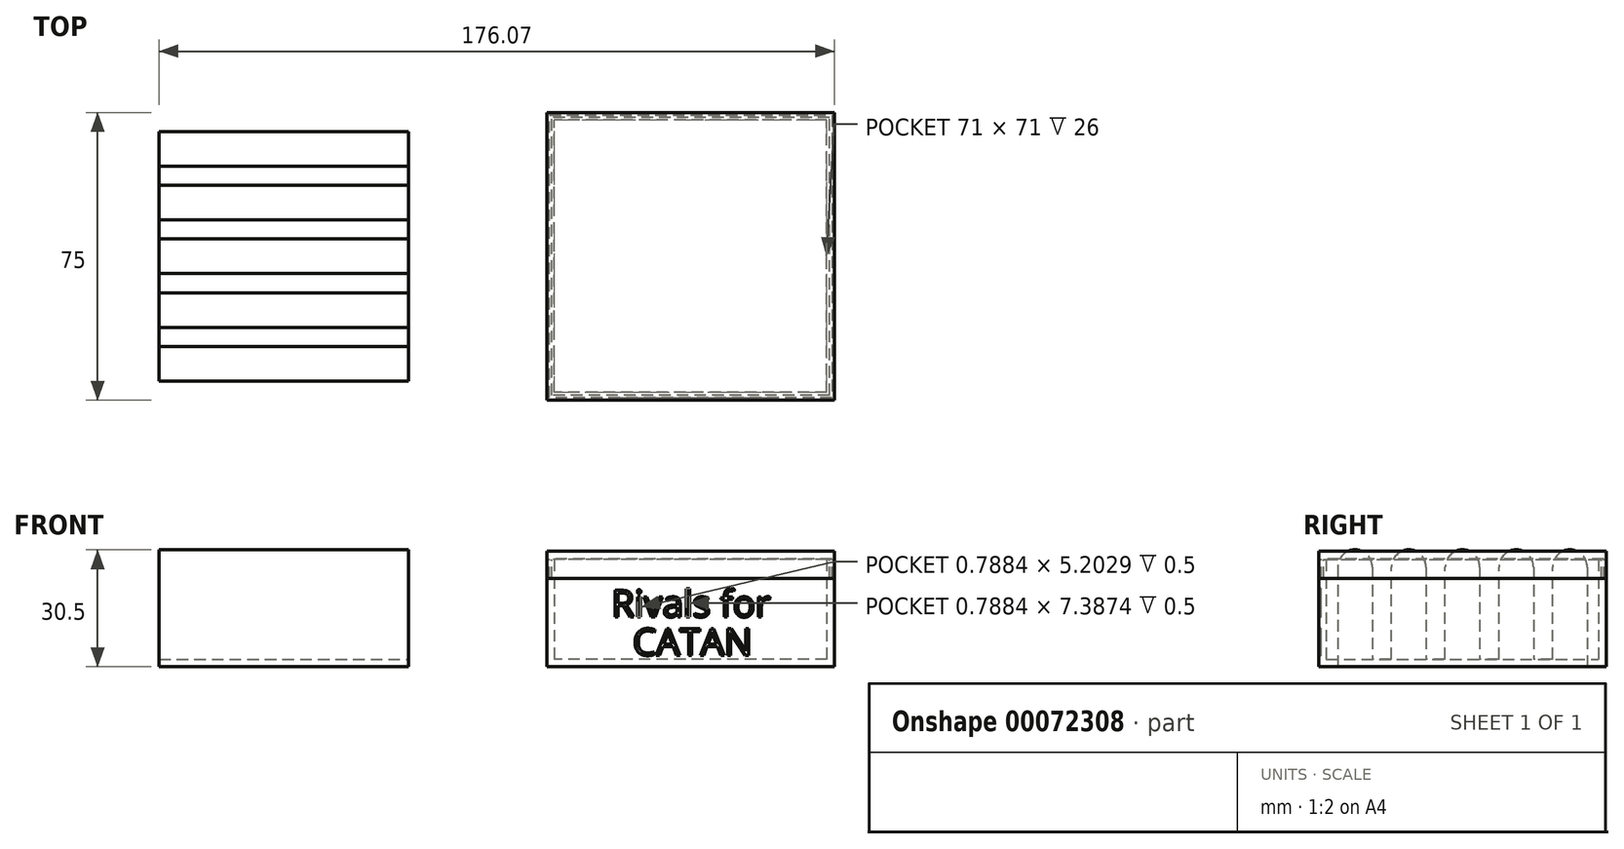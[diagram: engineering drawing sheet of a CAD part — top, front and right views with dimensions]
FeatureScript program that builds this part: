
annotation { "Feature Type Name" : "Feature", "Feature Type Description" : "" }
export const myFeature = defineFeature(function(context is Context, id is Id, definition is map)
    precondition{}
    {
        {
            var Q0;
            Q0=qCreatedBy(makeId("Top.planeOp"),FACE);
            var sketch = newSketch(context, id + "F0", { "sketchPlane" : qUnion([Q0])});
            skLineSegment(sketch, "E0.rect.bottom", {"start": v(37.5, -37.5) * mm, "end": v(-37.5, -37.5) * mm});
            skLineSegment(sketch, "E0.rect.top", {"start": v(37.5, 37.5) * mm, "end": v(-37.5, 37.5) * mm});
            skLineSegment(sketch, "E0.rect.left", {"start": v(37.5, -37.5) * mm, "end": v(37.5, 37.5) * mm});
            skLineSegment(sketch, "E0.rect.right", {"start": v(-37.5, -37.5) * mm, "end": v(-37.5, 37.5) * mm});
            skPoint(sketch, "E0.rect.middle", {"position": v(0, 0) * mm});
            skLineSegment(sketch, "E1", {"start": v(-37.5, 37.5) * mm, "end": v(37.5, -37.5) * mm, "construction": true});
            skLineSegment(sketch, "E2", {"start": v(0, 0) * mm, "end": v(-106.07, 0) * mm, "construction": true});
            skLineSegment(sketch, "E3.rect.bottom", {"start": v(-73.57, 32.5) * mm, "end": v(-138.57, 32.5) * mm});
            skLineSegment(sketch, "E3.rect.top", {"start": v(-73.57, -32.5) * mm, "end": v(-138.57, -32.5) * mm});
            skLineSegment(sketch, "E3.rect.left", {"start": v(-73.57, 32.5) * mm, "end": v(-73.57, -32.5) * mm});
            skLineSegment(sketch, "E3.rect.right", {"start": v(-138.57, 32.5) * mm, "end": v(-138.57, -32.5) * mm});
            skPoint(sketch, "E3.rect.middle", {"position": v(-106.07, 0) * mm});
            skSolve(sketch);
        }
        {
            var Q0;
            Q0 = qSketchRegion(id + "F0", true);
            extrude(context, id + "F1", {"entities" : qUnion([Q0]), "depth" : 2 * mm});
        }
        {
            var Q0;
            Q0=makeQuery(id+"F1.opExtrude","CAP_FACE",FACE,{"disambiguationData":[OSD([sQuery(id+"F0.wireOp",EDGE,"E0.rect.bottom"),sQuery(id+"F0.wireOp",EDGE,"E0.rect.top"),sQuery(id+"F0.wireOp",EDGE,"E0.rect.left"),sQuery(id+"F0.wireOp",EDGE,"E0.rect.right")])],"isStart":false});
            var sketch = newSketch(context, id + "F2", { "sketchPlane" : qUnion([Q0])});
            skLineSegment(sketch, "E4.rect.bottom", {"start": v(35.5, -35.5) * mm, "end": v(-35.5, -35.5) * mm});
            skLineSegment(sketch, "E4.rect.top", {"start": v(35.5, 35.5) * mm, "end": v(-35.5, 35.5) * mm});
            skLineSegment(sketch, "E4.rect.left", {"start": v(35.5, -35.5) * mm, "end": v(35.5, 35.5) * mm});
            skLineSegment(sketch, "E4.rect.right", {"start": v(-35.5, -35.5) * mm, "end": v(-35.5, 35.5) * mm});
            skPoint(sketch, "E4.rect.middle", {"position": v(0, 0) * mm});
            skLineSegment(sketch, "E5.0.0", {"start": v(-37.5, -37.5) * mm, "end": v(37.5, -37.5) * mm});
            skLineSegment(sketch, "E5.0.1", {"start": v(37.5, -37.5) * mm, "end": v(37.5, 37.5) * mm});
            skLineSegment(sketch, "E5.0.2", {"start": v(37.5, 37.5) * mm, "end": v(-37.5, 37.5) * mm});
            skLineSegment(sketch, "E5.0.3", {"start": v(-37.5, 37.5) * mm, "end": v(-37.5, -37.5) * mm});
            skLineSegment(sketch, "E6", {"start": v(0, 35.5) * mm, "end": v(0, 37.5) * mm, "construction": true});
            skSolve(sketch);
        }
        {
            var Q0;
            Q0 = qSketchRegion(id + "F2", true);
            extrude(context, id + "F3", {"entities" : qUnion([Q0]), "operationType" : NewBodyOperationType.ADD, "depth" : 26 * mm});
        }
        {
            var Q0;
            Q0=makeQuery(id+"F3.opExtrude","CAP_FACE",FACE,{"disambiguationData":[OSD([sQuery(id+"F2.wireOp",EDGE,"E4.rect.bottom"),sQuery(id+"F2.wireOp",EDGE,"E4.rect.top"),sQuery(id+"F2.wireOp",EDGE,"E4.rect.left"),sQuery(id+"F2.wireOp",EDGE,"E4.rect.right"),sQuery(id+"F2.wireOp",EDGE,"E5.0.0"),sQuery(id+"F2.wireOp",EDGE,"E5.0.1"),sQuery(id+"F2.wireOp",EDGE,"E5.0.2"),sQuery(id+"F2.wireOp",EDGE,"E5.0.3")])],"isStart":false});
            var sketch = newSketch(context, id + "F4", { "sketchPlane" : qUnion([Q0])});
            skLineSegment(sketch, "E7.0", {"start": v(-37.5, -37.5) * mm, "end": v(-37.5, 37.5) * mm});
            skLineSegment(sketch, "E8.0", {"start": v(37.5, -37.5) * mm, "end": v(-37.5, -37.5) * mm});
            skLineSegment(sketch, "E9.0", {"start": v(37.5, -37.5) * mm, "end": v(37.5, 37.5) * mm});
            skLineSegment(sketch, "E10.0", {"start": v(37.5, 37.5) * mm, "end": v(-37.5, 37.5) * mm});
            skLineSegment(sketch, "E11.0", {"start": v(-36.2, -36.2) * mm, "end": v(-36.2, 36.2) * mm});
            skLineSegment(sketch, "E11.1", {"start": v(36.2, -36.2) * mm, "end": v(-36.2, -36.2) * mm});
            skLineSegment(sketch, "E11.2", {"start": v(36.2, -36.2) * mm, "end": v(36.2, 36.2) * mm});
            skLineSegment(sketch, "E11.3", {"start": v(36.2, 36.2) * mm, "end": v(-36.2, 36.2) * mm});
            skSolve(sketch);
        }
        {
            var Q0;
            Q0 = qSketchRegion(id + "F4", true);
            extrude(context, id + "F5", {"entities" : qUnion([Q0]), "operationType" : NewBodyOperationType.REMOVE, "oppositeDirection" : true, "depth" : 5 * mm});
        }
        {
            var Q0;
            Q0=makeQuery(id+"F3.opExtrude","CAP_FACE",FACE,{"disambiguationData":[OSD([sQuery(id+"F2.wireOp",EDGE,"E4.rect.bottom"),sQuery(id+"F2.wireOp",EDGE,"E4.rect.top"),sQuery(id+"F2.wireOp",EDGE,"E4.rect.left"),sQuery(id+"F2.wireOp",EDGE,"E4.rect.right"),sQuery(id+"F2.wireOp",EDGE,"E5.0.0"),sQuery(id+"F2.wireOp",EDGE,"E5.0.1"),sQuery(id+"F2.wireOp",EDGE,"E5.0.2"),sQuery(id+"F2.wireOp",EDGE,"E5.0.3")])],"isStart":false});
            cPlane(context, id + "F6", {"entities" : qUnion([Q0]), "cplaneType" : CPlaneType.OFFSET, "offset" : .1 * mm, "width" : 150 * mm, "height" : 150 * mm});
        }
        {
            var Q0;
            Q0=qCreatedBy(id+"F6.planeOp",FACE);
            var sketch = newSketch(context, id + "F7", { "sketchPlane" : qUnion([Q0])});
            skPoint(sketch, "E12.0", {"position": v(37.5, -37.5) * mm});
            skLineSegment(sketch, "E13.rect.bottom", {"start": v(37.5, -37.5) * mm, "end": v(-37.5, -37.5) * mm});
            skLineSegment(sketch, "E13.rect.top", {"start": v(37.5, 37.5) * mm, "end": v(-37.5, 37.5) * mm});
            skLineSegment(sketch, "E13.rect.left", {"start": v(37.5, -37.5) * mm, "end": v(37.5, 37.5) * mm});
            skLineSegment(sketch, "E13.rect.right", {"start": v(-37.5, -37.5) * mm, "end": v(-37.5, 37.5) * mm});
            skPoint(sketch, "E13.rect.middle", {"position": v(0, 0) * mm});
            skSolve(sketch);
        }
        {
            var Q0;
            Q0 = qSketchRegion(id + "F7", true);
            extrude(context, id + "F8", {"entities" : qUnion([Q0]), "depth" : 2 * mm});
        }
        {
            var Q0;
            Q0=makeQuery(id+"F8.opExtrude","CAP_FACE",FACE,{"disambiguationData":[OSD([sQuery(id+"F7.wireOp",EDGE,"E13.rect.bottom"),sQuery(id+"F7.wireOp",EDGE,"E13.rect.top"),sQuery(id+"F7.wireOp",EDGE,"E13.rect.left"),sQuery(id+"F7.wireOp",EDGE,"E13.rect.right")])],"isStart":true});
            var sketch = newSketch(context, id + "F9", { "sketchPlane" : qUnion([Q0])});
            skLineSegment(sketch, "E14.0.0", {"start": v(37.5, 37.5) * mm, "end": v(-37.5, 37.5) * mm});
            skLineSegment(sketch, "E14.0.1", {"start": v(-37.5, 37.5) * mm, "end": v(-37.5, -37.5) * mm});
            skLineSegment(sketch, "E14.0.2", {"start": v(-37.5, -37.5) * mm, "end": v(37.5, -37.5) * mm});
            skLineSegment(sketch, "E14.0.3", {"start": v(37.5, -37.5) * mm, "end": v(37.5, 37.5) * mm});
            skLineSegment(sketch, "E15.0", {"start": v(36.8, 36.8) * mm, "end": v(-36.8, 36.8) * mm});
            skLineSegment(sketch, "E15.1", {"start": v(36.8, -36.8) * mm, "end": v(36.8, 36.8) * mm});
            skLineSegment(sketch, "E15.2", {"start": v(-36.8, -36.8) * mm, "end": v(36.8, -36.8) * mm});
            skLineSegment(sketch, "E15.3", {"start": v(-36.8, 36.8) * mm, "end": v(-36.8, -36.8) * mm});
            skSolve(sketch);
        }
        {
            var Q0;
            Q0 = qSketchRegion(id + "F9", true);
            extrude(context, id + "F10", {"entities" : qUnion([Q0]), "operationType" : NewBodyOperationType.ADD, "depth" : 5 * mm});
        }
        {
            var Q0;
            Q0=makeQuery(id+"F3.boolean.opBoolean","MERGE",FACE,{"derivedFrom":[makeQuery(id+"F1.opExtrude","SWEPT_FACE",FACE,{"disambiguationData":[OSD([sQuery(id+"F0.wireOp",EDGE,"E0.rect.bottom")])]}),makeQuery(id+"F3.opExtrude","SWEPT_FACE",FACE,{"disambiguationData":[OSD([sQuery(id+"F2.wireOp",EDGE,"E5.0.0")])]})]});
            var sketch = newSketch(context, id + "F11", { "sketchPlane" : qUnion([Q0])});
            skText(sketch, "E16", { "text": "Rivals for", "fontName": "OpenSans-Regular.ttf"});
            skLineSegment(sketch, "E17", {"start": v(37.5, 23) * mm, "end": v(-37.5, 0) * mm, "construction": true});
            skPoint(sketch, "E18", {"position": v(0, 16.5) * mm});
            skPoint(sketch, "E19", {"position": v(0, 11.5) * mm});
            skLineSegment(sketch, "E20", {"start": v(0, 16.5) * mm, "end": v(0, 6.5) * mm, "construction": true});
            skText(sketch, "E21", { "text": "CATAN", "fontName": "OpenSans-Regular.ttf"});
            const initialGuessF11  = {"E16": [-0.02068, 0.013, 1, 0, 0.007], "E21": [-0.0151, 0.003, 1, 0, 0.007]};
            skSetInitialGuess(sketch, initialGuessF11);
            skSolve(sketch);
        }
        {
            var Q0;
            Q0 = qSketchRegion(id + "F11", true);
            extrude(context, id + "F12", {"entities" : qUnion([Q0]), "operationType" : NewBodyOperationType.REMOVE, "oppositeDirection" : true, "depth" : .5 * mm});
        }
        {
            var Q0;
            Q0=makeQuery(id+"F1.opExtrude","SWEPT_FACE",FACE,{"disambiguationData":[OSD([sQuery(id+"F0.wireOp",EDGE,"E3.rect.left")])]});
            var sketch = newSketch(context, id + "F13", { "sketchPlane" : qUnion([Q0])});
            skLineSegment(sketch, "E22", {"start": v(-32.5, 2) * mm, "end": v(-32.5, 26) * mm});
            skArc(sketch, "E23", {"start": v(-23.5, 26) * mm, "mid": v(-28, 30.5) * mm, "end": v(-32.5, 26) * mm});
            skLineSegment(sketch, "E24", {"start": v(-23.5, 26) * mm, "end": v(-23.5, 2) * mm});
            skLineSegment(sketch, "E25", {"start": v(-23.5, 2) * mm, "end": v(-32.5, 2) * mm});
            skLineSegment(sketch, "E26.1.0.0", {"start": v(-9.5, 2) * mm, "end": v(-18.5, 2) * mm});
            skLineSegment(sketch, "E26.1.0.1", {"start": v(-18.5, 2) * mm, "end": v(-18.5, 26) * mm});
            skArc(sketch, "E26.1.0.2", {"start": v(-9.5, 26) * mm, "mid": v(-14, 30.5) * mm, "end": v(-18.5, 26) * mm});
            skLineSegment(sketch, "E26.1.0.3", {"start": v(-9.5, 26) * mm, "end": v(-9.5, 2) * mm});
            skLineSegment(sketch, "E26.2.0.0", {"start": v(4.5, 2) * mm, "end": v(-4.5, 2) * mm});
            skLineSegment(sketch, "E26.2.0.1", {"start": v(-4.5, 2) * mm, "end": v(-4.5, 26) * mm});
            skArc(sketch, "E26.2.0.2", {"start": v(4.5, 26) * mm, "mid": v(0, 30.5) * mm, "end": v(-4.5, 26) * mm});
            skLineSegment(sketch, "E26.2.0.3", {"start": v(4.5, 26) * mm, "end": v(4.5, 2) * mm});
            skLineSegment(sketch, "E26.3.0.0", {"start": v(18.5, 2) * mm, "end": v(9.5, 2) * mm});
            skLineSegment(sketch, "E26.3.0.1", {"start": v(9.5, 2) * mm, "end": v(9.5, 26) * mm});
            skArc(sketch, "E26.3.0.2", {"start": v(18.5, 26) * mm, "mid": v(14, 30.5) * mm, "end": v(9.5, 26) * mm});
            skLineSegment(sketch, "E26.3.0.3", {"start": v(18.5, 26) * mm, "end": v(18.5, 2) * mm});
            skLineSegment(sketch, "E26.4.0.0", {"start": v(32.5, 2) * mm, "end": v(23.5, 2) * mm});
            skLineSegment(sketch, "E26.4.0.1", {"start": v(23.5, 2) * mm, "end": v(23.5, 26) * mm});
            skArc(sketch, "E26.4.0.2", {"start": v(32.5, 26) * mm, "mid": v(28, 30.5) * mm, "end": v(23.5, 26) * mm});
            skLineSegment(sketch, "E26.4.0.3", {"start": v(32.5, 26) * mm, "end": v(32.5, 2) * mm});
            skLineSegment(sketch, "E26.direction1", {"start": v(-32.5, 2) * mm, "end": v(-18.5, 2) * mm, "construction": true});
            skSolve(sketch);
        }
        {
            var Q0;
            Q0=makeQuery(id+"F13.imprint","IMPRINT",FACE,{"disambiguationData":[TD([[makeQuery(id+"F13.imprint","IMPRINT",EDGE,{"derivedFrom":sQuery(id+"F13.wireOp",EDGE,"E22")}),-1.0]])]});
            var Q1;
            Q1=makeQuery(id+"F13.imprint","IMPRINT",FACE,{"disambiguationData":[TD([[makeQuery(id+"F13.imprint","IMPRINT",EDGE,{"derivedFrom":sQuery(id+"F13.wireOp",EDGE,"E26.1.0.0")}),-1.0]])]});
            var Q2;
            Q2=makeQuery(id+"F13.imprint","IMPRINT",FACE,{"disambiguationData":[TD([[makeQuery(id+"F13.imprint","IMPRINT",EDGE,{"derivedFrom":sQuery(id+"F13.wireOp",EDGE,"E26.2.0.0")}),-1.0]])]});
            var Q3;
            Q3=makeQuery(id+"F13.imprint","IMPRINT",FACE,{"disambiguationData":[TD([[makeQuery(id+"F13.imprint","IMPRINT",EDGE,{"derivedFrom":sQuery(id+"F13.wireOp",EDGE,"E26.3.0.0")}),-1.0]])]});
            var Q4;
            {var subQ1=sQuery(id+"F13.wireOp",EDGE,"E26.4.0.1");Q4=makeQuery(id+"F13.imprint","IMPRINT",FACE,{"disambiguationData":[TD([[makeQuery(id+"F13.imprint","IMPRINT",EDGE,{"derivedFrom":subQ1}),-1.0]])]});}
            extrude(context, id + "F14", {"entities" : qUnion([Q0, Q1, Q2, Q3, Q4]), "operationType" : NewBodyOperationType.ADD, "oppositeDirection" : true, "depth" : 65 * mm});
        }
    });
